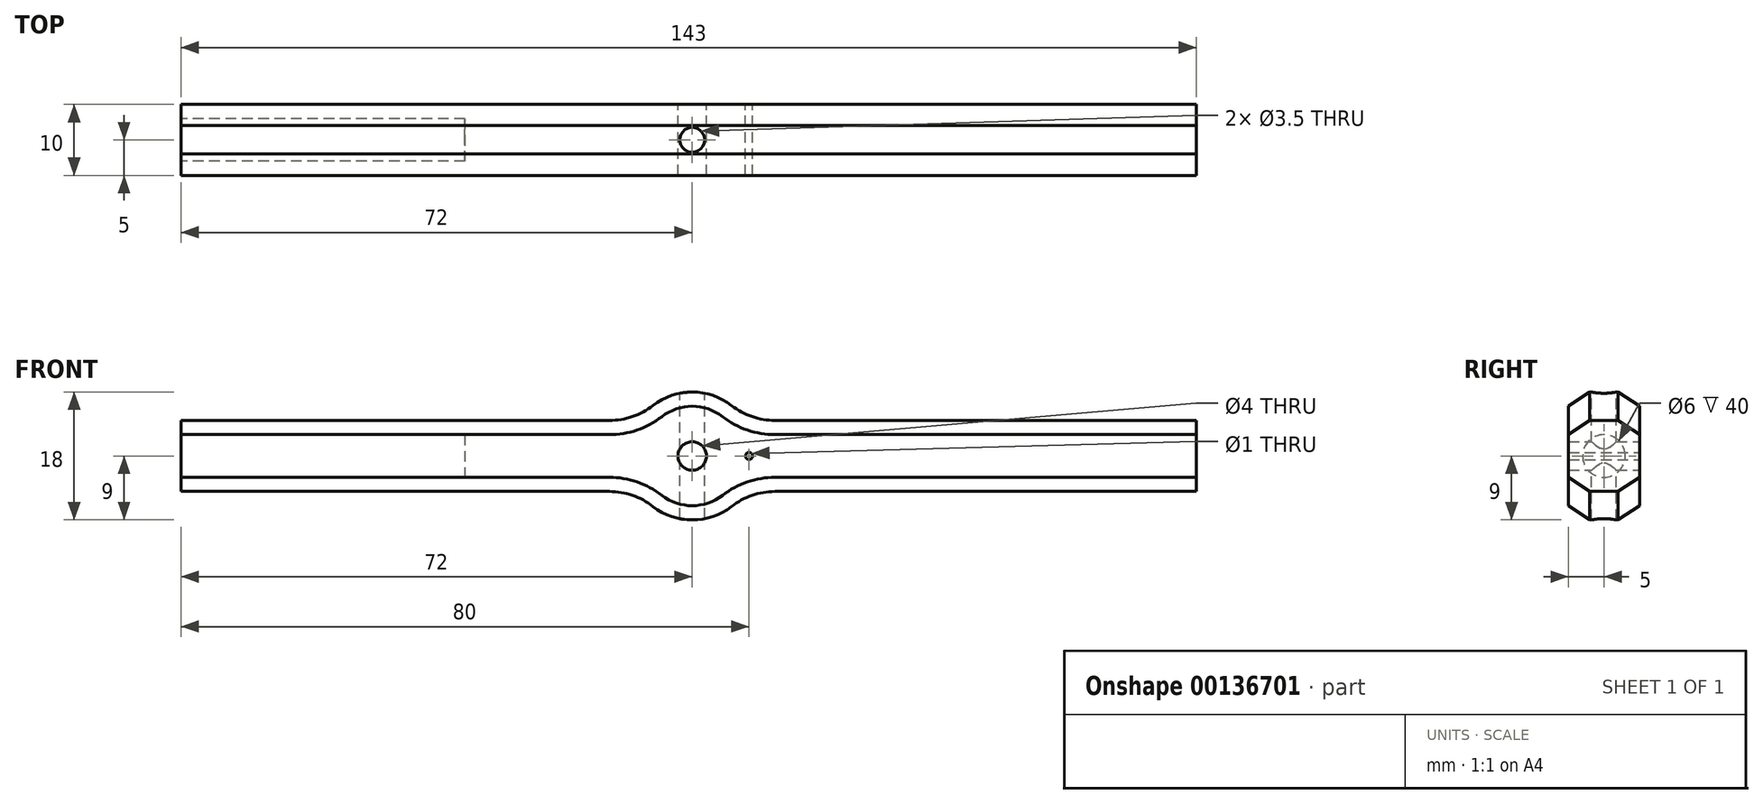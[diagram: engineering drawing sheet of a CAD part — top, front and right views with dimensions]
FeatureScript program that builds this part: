
annotation { "Feature Type Name" : "Feature", "Feature Type Description" : "" }
export const myFeature = defineFeature(function(context is Context, id is Id, definition is map)
    precondition{}
    {
        {
            var Q0;
            Q0=qCreatedBy(makeId("Front.planeOp"),FACE);
            var sketch = newSketch(context, id + "F0", { "sketchPlane" : qUnion([Q0])});
            skCircle(sketch, "E0", {"center": v(0, 0) * mm, "radius": 2 * mm});
            skLineSegment(sketch, "E1.bottom", {"start": v(7.48, 5) * mm, "end": v(71, 5) * mm});
            skLineSegment(sketch, "E1.top", {"start": v(7.48, -5) * mm, "end": v(71, -5) * mm});
            skLineSegment(sketch, "E1.left", {"start": v(7.48, 5) * mm, "end": v(7.48, -5) * mm, "construction": true});
            skLineSegment(sketch, "E1.right", {"start": v(71, 5) * mm, "end": v(71, -5) * mm});
            skLineSegment(sketch, "E2.bottom", {"start": v(-7.48, 5) * mm, "end": v(-72, 5) * mm});
            skLineSegment(sketch, "E2.top", {"start": v(-7.48, -5) * mm, "end": v(-72, -5) * mm});
            skLineSegment(sketch, "E2.left", {"start": v(-7.48, 5) * mm, "end": v(-7.48, -5) * mm, "construction": true});
            skLineSegment(sketch, "E2.right", {"start": v(-72, 5) * mm, "end": v(-72, -5) * mm});
            skLineSegment(sketch, "E3", {"start": v(-7.48, 5) * mm, "end": v(7.48, 5) * mm, "construction": true});
            skLineSegment(sketch, "E4", {"start": v(-7.48, -5) * mm, "end": v(7.48, -5) * mm, "construction": true});
            skArc(sketch, "E5", {"start": v(-7.48, 5) * mm, "mid": v(-9, 0) * mm, "end": v(-7.48, -5) * mm, "construction": true});
            skArc(sketch, "E6", {"start": v(-7.48, -5) * mm, "mid": v(0, -9) * mm, "end": v(7.48, -5) * mm});
            skArc(sketch, "E7", {"start": v(7.48, -5) * mm, "mid": v(9, 0) * mm, "end": v(7.48, 5) * mm, "construction": true});
            skArc(sketch, "E8", {"start": v(7.48, 5) * mm, "mid": v(0, 9) * mm, "end": v(-7.48, 5) * mm});
            skCircle(sketch, "E9", {"center": v(8, 0) * mm, "radius": 0.5 * mm});
            skSolve(sketch);
        }
        {
            var Q0;
            Q0=qSketchRegion(id+"F0",true);
            extrude(context, id + "F1", {"entities" : qUnion([Q0]), "depth" : 10 * mm});
        }
        {
            var Q0;
            Q0=makeQuery(id+"F1.opExtrude","SWEPT_FACE",FACE,{"disambiguationData":[OSD([sQuery(id+"F0.wireOp",EDGE,"E2.right")])]});
            var sketch = newSketch(context, id + "F2", { "sketchPlane" : qUnion([Q0])});
            skCircle(sketch, "E10", {"center": v(5, 0) * mm, "radius": 3 * mm});
            skLineSegment(sketch, "E11", {"start": v(0, 5) * mm, "end": v(10, -5) * mm, "construction": true});
            skSolve(sketch);
        }
        {
            var Q0;
            Q0=qSketchRegion(id+"F2",true);
            extrude(context, id + "F3", {"entities" : qUnion([Q0]), "operationType" : NewBodyOperationType.REMOVE, "oppositeDirection" : true, "depth" : 40 * mm});
        }
        {
            var Q0;
            Q0=qCreatedBy(makeId("Top.planeOp"),FACE);
            var sketch = newSketch(context, id + "F4", { "sketchPlane" : qUnion([Q0])});
            skCircle(sketch, "E12", {"center": v(0, -5) * mm, "radius": 1.75 * mm});
            skSolve(sketch);
        }
        {
            var Q0;
            Q0=qSketchRegion(id+"F4",true);
            extrude(context, id + "F5", {"entities" : qUnion([Q0]), "operationType" : NewBodyOperationType.REMOVE, "endBound" : BoundingType.THROUGH_ALL, "oppositeDirection" : true, "depth" : 25 * mm, "hasSecondDirection" : true, "secondDirectionBound" : SecondDirectionBoundingType.THROUGH_ALL, "secondDirectionOppositeDirection" : false, "secondDirectionDepth" : 25 * mm});
        }
        {
            var Q0;
            Q0=makeQuery(id+"F1.opExtrude","SWEPT_EDGE",EDGE,{"disambiguationData":[OSD([sQuery(id+"F0.wireOp",EDGE,"E2.bottom"),sQuery(id+"F0.wireOp",EDGE,"E8")])]});
            var Q1;
            Q1=makeQuery(id+"F1.opExtrude","SWEPT_EDGE",EDGE,{"disambiguationData":[OSD([sQuery(id+"F0.wireOp",EDGE,"E1.bottom"),sQuery(id+"F0.wireOp",EDGE,"E8")])]});
            var Q2;
            Q2=makeQuery(id+"F1.opExtrude","SWEPT_EDGE",EDGE,{"disambiguationData":[OSD([sQuery(id+"F0.wireOp",EDGE,"E1.top"),sQuery(id+"F0.wireOp",EDGE,"E6")])]});
            var Q3;
            Q3=makeQuery(id+"F1.opExtrude","SWEPT_EDGE",EDGE,{"disambiguationData":[OSD([sQuery(id+"F0.wireOp",EDGE,"E2.top"),sQuery(id+"F0.wireOp",EDGE,"E6")])]});
            var Q4;
            Q4=makeQuery(id+"F8.boolean.opBoolean","INTERSECT",EDGE,{"derivedFrom":[makeQuery(id+"F1.opExtrude","SWEPT_FACE",FACE,{"disambiguationData":[OSD([sQuery(id+"F0.wireOp",EDGE,"E1.bottom")])]}),makeQuery(id+"F8.opExtrude","SWEPT_FACE",FACE,{"disambiguationData":[OSD([sQuery(id+"FqUPChPoVJXvrYf_1.wireOp",EDGE,"aNJPpA9v-C1Hh-cPNh-mDaa-UnRmCzPOYgnN")])]})]});
            var Q5;
            Q5=makeQuery(id+"F8.boolean.opBoolean","INTERSECT",EDGE,{"derivedFrom":[makeQuery(id+"F1.opExtrude","SWEPT_FACE",FACE,{"disambiguationData":[OSD([sQuery(id+"F0.wireOp",EDGE,"E2.bottom")])]}),makeQuery(id+"F8.opExtrude","SWEPT_FACE",FACE,{"disambiguationData":[OSD([sQuery(id+"FqUPChPoVJXvrYf_1.wireOp",EDGE,"aNJPpA9v-C1Hh-cPNh-mDaa-UnRmCzPOYgnN")])]})]});
            var Q6;
            Q6=makeQuery(id+"F8.boolean.opBoolean","INTERSECT",EDGE,{"derivedFrom":[makeQuery(id+"F1.opExtrude","SWEPT_FACE",FACE,{"disambiguationData":[OSD([sQuery(id+"F0.wireOp",EDGE,"E2.top")])]}),makeQuery(id+"F8.opExtrude","SWEPT_FACE",FACE,{"disambiguationData":[OSD([sQuery(id+"FqUPChPoVJXvrYf_1.wireOp",EDGE,"aNJPpA9v-C1Hh-cPNh-mDaa-UnRmCzPOYgnN")])]})]});
            var Q7;
            Q7=makeQuery(id+"F8.boolean.opBoolean","INTERSECT",EDGE,{"derivedFrom":[makeQuery(id+"F1.opExtrude","SWEPT_FACE",FACE,{"disambiguationData":[OSD([sQuery(id+"F0.wireOp",EDGE,"E1.top")])]}),makeQuery(id+"F8.opExtrude","SWEPT_FACE",FACE,{"disambiguationData":[OSD([sQuery(id+"FqUPChPoVJXvrYf_1.wireOp",EDGE,"aNJPpA9v-C1Hh-cPNh-mDaa-UnRmCzPOYgnN")])]})]});
            fillet(context, id + "F6", {"entities" : qUnion([Q0, Q1, Q2, Q3, Q4, Q5, Q6, Q7]), "radius" : 10 * mm, "tangentPropagation" : true, "allowEdgeOverflow" : false});
        }
        {
            var Q0;
            Q0=makeQuery(id+"F1.opExtrude","CAP_EDGE",EDGE,{"disambiguationData":[OSD([sQuery(id+"F0.wireOp",EDGE,"E2.bottom")])],"isStart":false});
            var Q1;
            Q1=makeQuery(id+"F1.opExtrude","CAP_EDGE",EDGE,{"disambiguationData":[OSD([sQuery(id+"F0.wireOp",EDGE,"E2.top")])],"isStart":false});
            var Q2;
            Q2=makeQuery(id+"F1.opExtrude","CAP_EDGE",EDGE,{"disambiguationData":[OSD([sQuery(id+"F0.wireOp",EDGE,"E2.bottom")])],"isStart":true});
            var Q3;
            Q3=makeQuery(id+"F1.opExtrude","CAP_EDGE",EDGE,{"disambiguationData":[OSD([sQuery(id+"F0.wireOp",EDGE,"E2.top")])],"isStart":true});
            chamfer(context, id + "F7", {"entities" : qUnion([Q0, Q1, Q2, Q3]), "chamferType" : ChamferType.TWO_OFFSETS, "width1" : 2 * mm, "oppositeDirection" : false, "width2" : 3 * mm, "tangentPropagation" : true});
        }
    });
